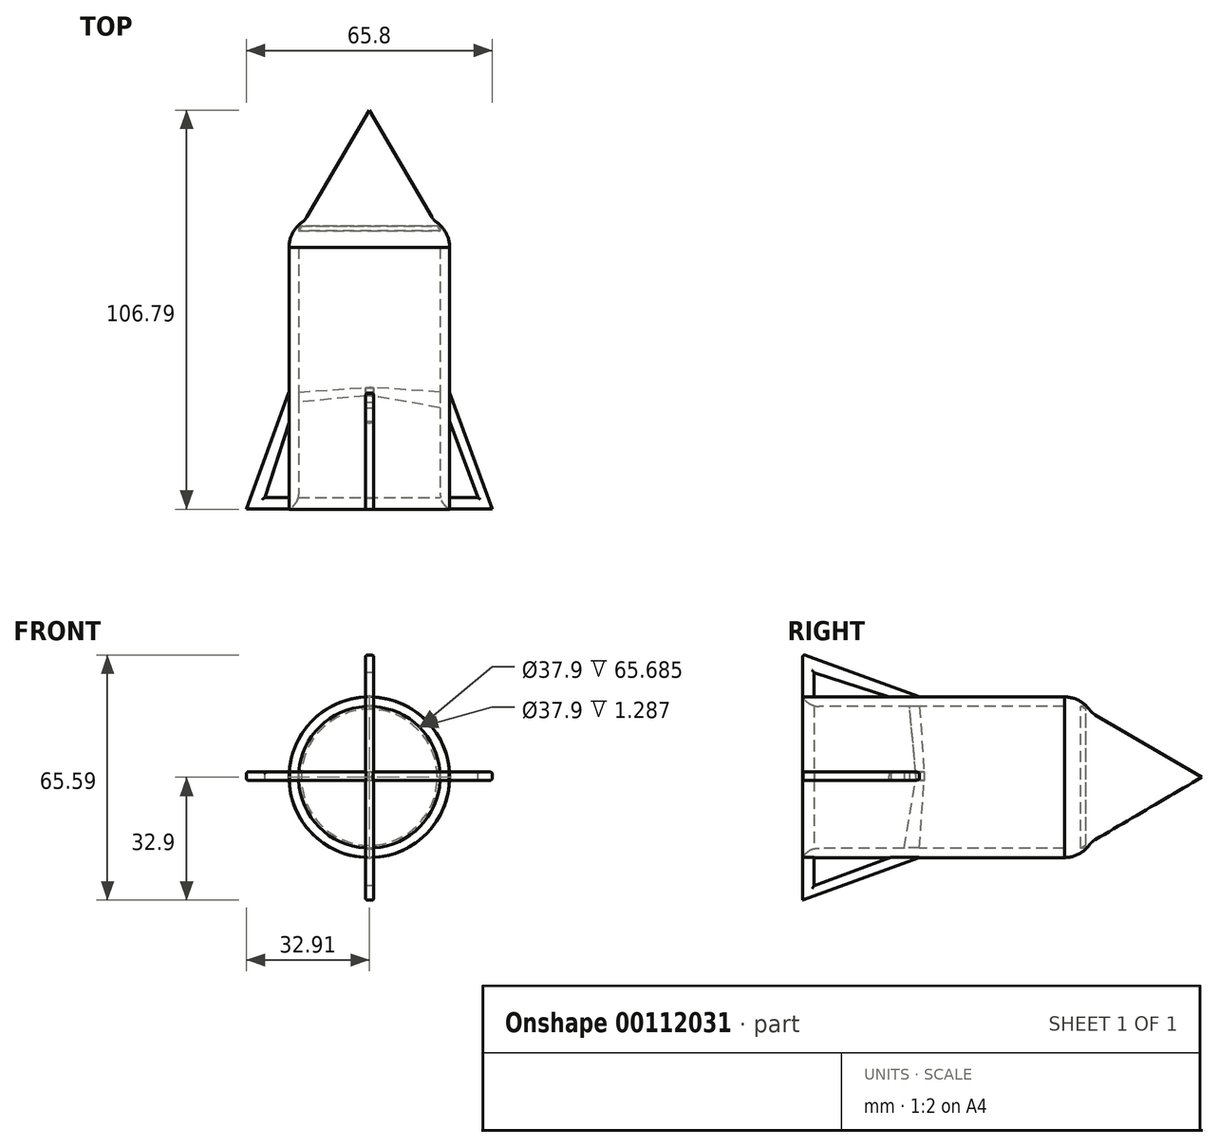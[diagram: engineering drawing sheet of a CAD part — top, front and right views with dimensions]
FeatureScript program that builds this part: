
annotation { "Feature Type Name" : "Feature", "Feature Type Description" : "" }
export const myFeature = defineFeature(function(context is Context, id is Id, definition is map)
    precondition{}
    {
        {
            var Q0;
            Q0=qCreatedBy(makeId("Front.planeOp"),FACE);
            var sketch = newSketch(context, id + "F0", { "sketchPlane" : qUnion([Q0])});
            skCircle(sketch, "E0", {"center": v(0, 0) * mm, "radius": 21.49 * mm});
            skSolve(sketch);
        }
        {
            var Q0;
            Q0 = qSketchRegion(id + "F0", true);
            extrude(context, id + "F1", {"entities" : qUnion([Q0]), "oppositeDirection" : true, "depth" : 78.3 * mm});
        }
        {
            var Q0;
            Q0=makeQuery(id+"F1.opExtrude","CAP_FACE",FACE,{"disambiguationData":[OSD([sQuery(id+"F0.wireOp",EDGE,"E0")])],"isStart":true});
            shell(context, id + "F2", {"entities" : qUnion([Q0]), "thickness" : 2.54 * mm});
        }
        {
            var Q0;
            {var subQ0=sQuery(id+"F0.wireOp",EDGE,"E0");Q0=makeQuery(id+"F2.opShell","OFFSET_EDGE",EDGE,{"disambiguationData":[OSD([subQ0]),TDD([makeQuery(id+"F1.opExtrude","CAP_EDGE",EDGE,{"disambiguationData":[OSD([subQ0])],"isStart":true})])]});}
            fillet(context, id + "F3", {"entities" : qUnion([Q0]), "radius" : 5.08 * mm, "tangentPropagation" : true, "allowEdgeOverflow" : false});
        }
        {
            var Q0;
            Q0=makeQuery(id+"F1.opExtrude","CAP_EDGE",EDGE,{"disambiguationData":[OSD([sQuery(id+"F0.wireOp",EDGE,"E0")])],"isStart":false});
            fillet(context, id + "F4", {"entities" : qUnion([Q0]), "radius" : 8.22 * mm, "tangentPropagation" : true, "allowEdgeOverflow" : false});
        }
        {
            var Q0;
            Q0=qCreatedBy(makeId("Right.planeOp"),FACE);
            var sketch = newSketch(context, id + "F5", { "sketchPlane" : qUnion([Q0])});
            skLineSegment(sketch, "E1", {"start": v(0, 0) * mm, "end": v(0, 32.9) * mm});
            skLineSegment(sketch, "E2", {"start": v(0, 32.9) * mm, "end": v(31.1, 21.54) * mm});
            skLineSegment(sketch, "E3", {"start": v(31.1, 21.54) * mm, "end": v(32.58, 0) * mm});
            skLineSegment(sketch, "E4", {"start": v(32.58, 0) * mm, "end": v(0, 0) * mm});
            skLineSegment(sketch, "E5.MirrorCS", {"start": v(0, -32.9) * mm, "end": v(31.1, -21.54) * mm});
            skLineSegment(sketch, "E6.MirrorCS", {"start": v(31.1, -21.54) * mm, "end": v(32.58, 0) * mm});
            skLineSegment(sketch, "E7.MirrorCS", {"start": v(0, 0) * mm, "end": v(0, -32.9) * mm});
            skLineSegment(sketch, "E8", {"start": v(28.54, 19.7) * mm, "end": v(3.06, 27.95) * mm});
            skLineSegment(sketch, "E9", {"start": v(3.06, 27.95) * mm, "end": v(3.06, -29.05) * mm});
            skLineSegment(sketch, "E10", {"start": v(3.06, -29.05) * mm, "end": v(26.9, -20.25) * mm});
            skLineSegment(sketch, "E11", {"start": v(26.9, -20.25) * mm, "end": v(30.38, 0) * mm});
            skLineSegment(sketch, "E12", {"start": v(30.38, 0) * mm, "end": v(28.54, 19.7) * mm});
            skSolve(sketch);
        }
        {
            var Q0;
            Q0 = qSketchRegion(id + "F5", true);
            var Q1;
            Q1=sQuery(id+"F5.wireOp",EDGE,"E1");
            var Q2;
            Q2=sQuery(id+"F5.wireOp",EDGE,"E2");
            var Q3;
            Q3=sQuery(id+"F5.wireOp",EDGE,"E6.MirrorCS");
            var Q4;
            Q4=sQuery(id+"F5.wireOp",EDGE,"E3");
            var Q5;
            Q5=sQuery(id+"F5.wireOp",EDGE,"E5.MirrorCS");
            var Q6;
            Q6=sQuery(id+"F5.wireOp",EDGE,"E7.MirrorCS");
            extrude(context, id + "F6", {"entities" : qUnion([Q0]), "operationType" : NewBodyOperationType.ADD, "surfaceEntities" : qUnion([Q1, Q2, Q3, Q4, Q5, Q6]), "depth" : 1.2 * mm, "hasSecondDirection" : true, "secondDirectionOppositeDirection" : true, "secondDirectionDepth" : 1.01 * mm});
        }
        {
            var Q0;
            Q0=qCreatedBy(makeId("Top.planeOp"),FACE);
            var sketch = newSketch(context, id + "F7", { "sketchPlane" : qUnion([Q0])});
            skLineSegment(sketch, "E13", {"start": v(-0.01, 0.1) * mm, "end": v(-32.91, 0.1) * mm});
            skLineSegment(sketch, "E14", {"start": v(-32.91, 0.1) * mm, "end": v(-21.55, 31.2) * mm});
            skLineSegment(sketch, "E15", {"start": v(-21.55, 31.2) * mm, "end": v(-0.01, 32.67) * mm});
            skLineSegment(sketch, "E16", {"start": v(-0.01, 32.67) * mm, "end": v(-0.01, 0.1) * mm});
            skLineSegment(sketch, "E17.MirrorCS", {"start": v(32.9, 0.1) * mm, "end": v(21.53, 31.2) * mm});
            skLineSegment(sketch, "E18.MirrorCS", {"start": v(21.53, 31.2) * mm, "end": v(-0.01, 32.67) * mm});
            skLineSegment(sketch, "E19.MirrorCS", {"start": v(-0.01, 0.1) * mm, "end": v(32.9, 0.1) * mm});
            skLineSegment(sketch, "E20", {"start": v(-19.72, 28.63) * mm, "end": v(-27.96, 3.16) * mm});
            skLineSegment(sketch, "E21", {"start": v(-27.96, 3.16) * mm, "end": v(29.04, 3.16) * mm});
            skLineSegment(sketch, "E22", {"start": v(29.04, 3.16) * mm, "end": v(20.24, 26.99) * mm});
            skLineSegment(sketch, "E23", {"start": v(20.24, 26.99) * mm, "end": v(-0.01, 30.47) * mm});
            skLineSegment(sketch, "E24", {"start": v(-0.01, 30.47) * mm, "end": v(-19.72, 28.63) * mm});
            skSolve(sketch);
        }
        {
            var Q0;
            Q0 = qSketchRegion(id + "F7", true);
            extrude(context, id + "F8", {"entities" : qUnion([Q0]), "operationType" : NewBodyOperationType.ADD, "oppositeDirection" : true, "depth" : 0.82 * mm, "hasSecondDirection" : true, "secondDirectionOppositeDirection" : false, "secondDirectionDepth" : 1.41 * mm});
        }
        {
            var Q0;
            Q0=qCreatedBy(makeId("Top.planeOp"),FACE);
            var sketch = newSketch(context, id + "F9", { "sketchPlane" : qUnion([Q0])});
            skLineSegment(sketch, "E25", {"start": v(-21.52, 70.08) * mm, "end": v(0, 70.08) * mm});
            skLineSegment(sketch, "E26", {"start": v(0, 70.08) * mm, "end": v(0, 106.8) * mm});
            skLineSegment(sketch, "E27", {"start": v(0, 106.8) * mm, "end": v(-21.52, 70.08) * mm});
            skSolve(sketch);
        }
        {
            var Q0;
            Q0 = qSketchRegion(id + "F9", true);
            var Q1;
            Q1=sQuery(id+"F9.wireOp",EDGE,"E26");
            revolve(context, id + "F10", {"operationType" : NewBodyOperationType.ADD, "entities" : qUnion([Q0]), "axis" : qUnion([Q1]), "revolveType" : RevolveType.FULL});
        }
        {
            var Q0;
            Q0=makeQuery(id+"F10.boolean.opBoolean","INTERSECT",EDGE,{"disambiguationData":[OD(0.0)],"derivedFrom":[makeQuery(id+"F4.opFillet","BLEND_FACE",FACE,{"disambiguationData":[OSD([sQuery(id+"F0.wireOp",EDGE,"E0")])]}),makeQuery(id+"F10.opRevolve","SWEPT_FACE",FACE,{"disambiguationData":[OSD([sQuery(id+"F9.wireOp",EDGE,"E27")])]})]});
            var Q1;
            Q1=makeQuery(id+"F10.boolean.opBoolean","INTERSECT",EDGE,{"disambiguationData":[OD(1.0)],"derivedFrom":[makeQuery(id+"F4.opFillet","BLEND_FACE",FACE,{"disambiguationData":[OSD([sQuery(id+"F0.wireOp",EDGE,"E0")])]}),makeQuery(id+"F10.opRevolve","SWEPT_FACE",FACE,{"disambiguationData":[OSD([sQuery(id+"F9.wireOp",EDGE,"E27")])]})]});
            fillet(context, id + "F11", {"entities" : qUnion([Q0, Q1]), "radius" : 5.08 * mm, "tangentPropagation" : true, "allowEdgeOverflow" : false});
        }
        {
            var Q0;
            {var subQ0=makeQuery(id+"F4.opFillet","BLEND_FACE",FACE,{"disambiguationData":[OSD([sQuery(id+"F0.wireOp",EDGE,"E0")])]});var subQ1=makeQuery(id+"F10.opRevolve","SWEPT_FACE",FACE,{"disambiguationData":[OSD([sQuery(id+"F9.wireOp",EDGE,"E27")])]});Q0=makeQuery(id+"F11.opFillet","BLEND_EDGE",EDGE,{"blendedFrom":[makeQuery(id+"F10.boolean.opBoolean","INTERSECT",EDGE,{"disambiguationData":[OD(1.0)],"derivedFrom":[subQ0,subQ1]}),makeQuery(id+"F10.boolean.opBoolean","SPLIT",FACE,{"disambiguationData":[TD([subQ0])],"derivedFrom":makeQuery(id+"F10.opRevolve","SWEPT_FACE",FACE,{"disambiguationData":[OSD([sQuery(id+"F9.wireOp",EDGE,"E25")])]})})],"blendedInto":[makeQuery(id+"F10.boolean.opBoolean","SPLIT",FACE,{"disambiguationData":[TD([subQ0])],"derivedFrom":makeQuery(id+"F10.opRevolve","SWEPT_FACE",FACE,{"disambiguationData":[OSD([sQuery(id+"F9.wireOp",EDGE,"E25")])]})})]});}
            fillet(context, id + "F12", {"entities" : qUnion([Q0]), "radius" : 5.08 * mm, "tangentPropagation" : true, "allowEdgeOverflow" : false});
        }
        {
            var Q0;
            Q0=makeQuery(id+"F6.opExtrude","CAP_EDGE",EDGE,{"disambiguationData":[OSD([sQuery(id+"F5.wireOp",EDGE,"E2")])],"isStart":false});
            var Q1;
            Q1=makeQuery(id+"F6.opExtrude","CAP_EDGE",EDGE,{"disambiguationData":[OSD([sQuery(id+"F5.wireOp",EDGE,"E2")])],"isStart":true});
            var Q2;
            Q2=makeQuery(id+"F6.opExtrude","SWEPT_FACE",FACE,{"disambiguationData":[OSD([sQuery(id+"F5.wireOp",EDGE,"E2")])]});
            var Q3;
            Q3=makeQuery(id+"F8.opExtrude","CAP_EDGE",EDGE,{"disambiguationData":[OSD([sQuery(id+"F7.wireOp",EDGE,"E17.MirrorCS")])],"isStart":true});
            var Q4;
            Q4=makeQuery(id+"F8.opExtrude","CAP_EDGE",EDGE,{"disambiguationData":[OSD([sQuery(id+"F7.wireOp",EDGE,"E17.MirrorCS")])],"isStart":false});
            var Q5;
            Q5=makeQuery(id+"F8.opExtrude","CAP_EDGE",EDGE,{"disambiguationData":[OSD([sQuery(id+"F7.wireOp",EDGE,"E14")])],"isStart":true});
            var Q6;
            Q6=makeQuery(id+"F8.opExtrude","CAP_EDGE",EDGE,{"disambiguationData":[OSD([sQuery(id+"F7.wireOp",EDGE,"E14")])],"isStart":false});
            var Q7;
            Q7=makeQuery(id+"F6.opExtrude","CAP_EDGE",EDGE,{"disambiguationData":[OSD([sQuery(id+"F5.wireOp",EDGE,"E5.MirrorCS")])],"isStart":false});
            var Q8;
            Q8=makeQuery(id+"F6.opExtrude","CAP_EDGE",EDGE,{"disambiguationData":[OSD([sQuery(id+"F5.wireOp",EDGE,"E5.MirrorCS")])],"isStart":true});
            var Q9;
            {var subQ0=sQuery(id+"F7.wireOp",EDGE,"E17.MirrorCS");var subQ1=sQuery(id+"F7.wireOp",EDGE,"E19.MirrorCS");var subQ2=sQuery(id+"F7.wireOp",EDGE,"E13");Q9=makeQuery(id+"F8.boolean.opBoolean","SPLIT",EDGE,{"disambiguationData":[TD([makeQuery(id+"F8.opExtrude","SWEPT_FACE",FACE,{"disambiguationData":[OSD([subQ0])]})])],"derivedFrom":makeQuery(id+"F8.opExtrude","CAP_EDGE",EDGE,{"disambiguationData":[OSD([subQ2,subQ1])],"isStart":true})});}
            var Q10;
            {var subQ0=sQuery(id+"F7.wireOp",EDGE,"E17.MirrorCS");var subQ1=sQuery(id+"F7.wireOp",EDGE,"E19.MirrorCS");var subQ2=sQuery(id+"F7.wireOp",EDGE,"E13");Q10=makeQuery(id+"F8.boolean.opBoolean","SPLIT",EDGE,{"disambiguationData":[TD([makeQuery(id+"F8.opExtrude","SWEPT_FACE",FACE,{"disambiguationData":[OSD([subQ0])]})])],"derivedFrom":makeQuery(id+"F8.opExtrude","CAP_EDGE",EDGE,{"disambiguationData":[OSD([subQ2,subQ1])],"isStart":false})});}
            var Q11;
            {var subQ0=sQuery(id+"F5.wireOp",EDGE,"E7.MirrorCS");var subQ1=sQuery(id+"F5.wireOp",EDGE,"E1");var subQ2=sQuery(id+"F5.wireOp",EDGE,"E2");var subQ3=sQuery(id+"F0.wireOp",EDGE,"E0");Q11=makeQuery(id+"F6.boolean.opBoolean","SPLIT",EDGE,{"disambiguationData":[TD([makeQuery(id+"F1.opExtrude","SWEPT_FACE",FACE,{"disambiguationData":[OSD([subQ3])]}),makeQuery(id+"F3.opFillet","BLEND_FACE",FACE,{"disambiguationData":[OSD([subQ3])]}),makeQuery(id+"F6.opExtrude","CAP_FACE",FACE,{"disambiguationData":[OSD([subQ1,subQ2,sQuery(id+"F5.wireOp",EDGE,"E3"),sQuery(id+"F5.wireOp",EDGE,"E6.MirrorCS"),subQ0,sQuery(id+"F5.wireOp",EDGE,"E5.MirrorCS"),sQuery(id+"F5.wireOp",EDGE,"E8"),sQuery(id+"F5.wireOp",EDGE,"E9"),sQuery(id+"F5.wireOp",EDGE,"E10"),sQuery(id+"F5.wireOp",EDGE,"E11"),sQuery(id+"F5.wireOp",EDGE,"E12")])],"isStart":false}),makeQuery(id+"F6.opExtrude","SWEPT_FACE",FACE,{"disambiguationData":[OSD([subQ1,subQ0])]}),makeQuery(id+"F6.opExtrude","SWEPT_FACE",FACE,{"disambiguationData":[OSD([subQ2])]})])],"derivedFrom":makeQuery(id+"F6.opExtrude","CAP_EDGE",EDGE,{"disambiguationData":[OSD([subQ1,subQ0])],"isStart":false})});}
            var Q12;
            {var subQ0=sQuery(id+"F5.wireOp",EDGE,"E7.MirrorCS");var subQ1=sQuery(id+"F5.wireOp",EDGE,"E1");var subQ2=sQuery(id+"F5.wireOp",EDGE,"E2");var subQ3=sQuery(id+"F0.wireOp",EDGE,"E0");Q12=makeQuery(id+"F6.boolean.opBoolean","SPLIT",EDGE,{"disambiguationData":[TD([makeQuery(id+"F1.opExtrude","SWEPT_FACE",FACE,{"disambiguationData":[OSD([subQ3])]}),makeQuery(id+"F3.opFillet","BLEND_FACE",FACE,{"disambiguationData":[OSD([subQ3])]}),makeQuery(id+"F6.opExtrude","CAP_FACE",FACE,{"disambiguationData":[OSD([subQ1,subQ2,sQuery(id+"F5.wireOp",EDGE,"E3"),sQuery(id+"F5.wireOp",EDGE,"E6.MirrorCS"),subQ0,sQuery(id+"F5.wireOp",EDGE,"E5.MirrorCS"),sQuery(id+"F5.wireOp",EDGE,"E8"),sQuery(id+"F5.wireOp",EDGE,"E9"),sQuery(id+"F5.wireOp",EDGE,"E10"),sQuery(id+"F5.wireOp",EDGE,"E11"),sQuery(id+"F5.wireOp",EDGE,"E12")])],"isStart":true}),makeQuery(id+"F6.opExtrude","SWEPT_FACE",FACE,{"disambiguationData":[OSD([subQ1,subQ0])]}),makeQuery(id+"F6.opExtrude","SWEPT_FACE",FACE,{"disambiguationData":[OSD([subQ2])]})])],"derivedFrom":makeQuery(id+"F6.opExtrude","CAP_EDGE",EDGE,{"disambiguationData":[OSD([subQ1,subQ0])],"isStart":true})});}
            var Q13;
            {var subQ0=sQuery(id+"F5.wireOp",EDGE,"E7.MirrorCS");var subQ1=sQuery(id+"F5.wireOp",EDGE,"E1");var subQ2=sQuery(id+"F5.wireOp",EDGE,"E5.MirrorCS");var subQ3=sQuery(id+"F0.wireOp",EDGE,"E0");Q13=makeQuery(id+"F6.boolean.opBoolean","SPLIT",EDGE,{"disambiguationData":[TD([makeQuery(id+"F1.opExtrude","SWEPT_FACE",FACE,{"disambiguationData":[OSD([subQ3])]}),makeQuery(id+"F3.opFillet","BLEND_FACE",FACE,{"disambiguationData":[OSD([subQ3])]}),makeQuery(id+"F6.opExtrude","CAP_FACE",FACE,{"disambiguationData":[OSD([subQ1,sQuery(id+"F5.wireOp",EDGE,"E2"),sQuery(id+"F5.wireOp",EDGE,"E3"),sQuery(id+"F5.wireOp",EDGE,"E6.MirrorCS"),subQ0,subQ2,sQuery(id+"F5.wireOp",EDGE,"E8"),sQuery(id+"F5.wireOp",EDGE,"E9"),sQuery(id+"F5.wireOp",EDGE,"E10"),sQuery(id+"F5.wireOp",EDGE,"E11"),sQuery(id+"F5.wireOp",EDGE,"E12")])],"isStart":true}),makeQuery(id+"F6.opExtrude","SWEPT_FACE",FACE,{"disambiguationData":[OSD([subQ1,subQ0])]}),makeQuery(id+"F6.opExtrude","SWEPT_FACE",FACE,{"disambiguationData":[OSD([subQ2])]})])],"derivedFrom":makeQuery(id+"F6.opExtrude","CAP_EDGE",EDGE,{"disambiguationData":[OSD([subQ1,subQ0])],"isStart":true})});}
            var Q14;
            {var subQ0=sQuery(id+"F7.wireOp",EDGE,"E19.MirrorCS");var subQ1=sQuery(id+"F7.wireOp",EDGE,"E14");var subQ2=sQuery(id+"F7.wireOp",EDGE,"E13");Q14=makeQuery(id+"F8.boolean.opBoolean","SPLIT",EDGE,{"disambiguationData":[TD([makeQuery(id+"F8.opExtrude","SWEPT_FACE",FACE,{"disambiguationData":[OSD([subQ1])]})])],"derivedFrom":makeQuery(id+"F8.opExtrude","CAP_EDGE",EDGE,{"disambiguationData":[OSD([subQ2,subQ0])],"isStart":false})});}
            var Q15;
            Q15=makeQuery(id+"F6.opExtrude","CAP_EDGE",EDGE,{"disambiguationData":[OSD([sQuery(id+"F5.wireOp",EDGE,"E8")])],"isStart":false});
            var Q16;
            Q16=makeQuery(id+"F8.opExtrude","CAP_EDGE",EDGE,{"disambiguationData":[OSD([sQuery(id+"F7.wireOp",EDGE,"E22")])],"isStart":true});
            var Q17;
            Q17=makeQuery(id+"F8.opExtrude","CAP_EDGE",EDGE,{"disambiguationData":[OSD([sQuery(id+"F7.wireOp",EDGE,"E22")])],"isStart":false});
            var Q18;
            {var subQ0=sQuery(id+"F7.wireOp",EDGE,"E21");var subQ1=sQuery(id+"F7.wireOp",EDGE,"E22");Q18=makeQuery(id+"F8.boolean.opBoolean","SPLIT",EDGE,{"disambiguationData":[TD([makeQuery(id+"F8.opExtrude","SWEPT_FACE",FACE,{"disambiguationData":[OSD([subQ1])]})])],"derivedFrom":makeQuery(id+"F8.opExtrude","CAP_EDGE",EDGE,{"disambiguationData":[OSD([subQ0])],"isStart":false})});}
            var Q19;
            {var subQ0=sQuery(id+"F5.wireOp",EDGE,"E9");var subQ1=sQuery(id+"F5.wireOp",EDGE,"E8");Q19=makeQuery(id+"F6.boolean.opBoolean","SPLIT",EDGE,{"disambiguationData":[TD([makeQuery(id+"F6.opExtrude","SWEPT_FACE",FACE,{"disambiguationData":[OSD([subQ1])]})])],"derivedFrom":makeQuery(id+"F6.opExtrude","CAP_EDGE",EDGE,{"disambiguationData":[OSD([subQ0])],"isStart":true})});}
            var Q20;
            {var subQ0=sQuery(id+"F5.wireOp",EDGE,"E9");var subQ1=sQuery(id+"F5.wireOp",EDGE,"E8");Q20=makeQuery(id+"F6.boolean.opBoolean","SPLIT",EDGE,{"disambiguationData":[TD([makeQuery(id+"F6.opExtrude","SWEPT_FACE",FACE,{"disambiguationData":[OSD([subQ1])]})])],"derivedFrom":makeQuery(id+"F6.opExtrude","CAP_EDGE",EDGE,{"disambiguationData":[OSD([subQ0])],"isStart":false})});}
            var Q21;
            {var subQ0=sQuery(id+"F7.wireOp",EDGE,"E21");var subQ1=sQuery(id+"F7.wireOp",EDGE,"E22");Q21=makeQuery(id+"F8.boolean.opBoolean","SPLIT",EDGE,{"disambiguationData":[TD([makeQuery(id+"F8.opExtrude","SWEPT_FACE",FACE,{"disambiguationData":[OSD([subQ1])]})])],"derivedFrom":makeQuery(id+"F8.opExtrude","CAP_EDGE",EDGE,{"disambiguationData":[OSD([subQ0])],"isStart":true})});}
            var Q22;
            {var subQ0=sQuery(id+"F7.wireOp",EDGE,"E21");var subQ1=sQuery(id+"F7.wireOp",EDGE,"E20");Q22=makeQuery(id+"F8.boolean.opBoolean","SPLIT",EDGE,{"disambiguationData":[TD([makeQuery(id+"F8.opExtrude","SWEPT_FACE",FACE,{"disambiguationData":[OSD([subQ1])]})])],"derivedFrom":makeQuery(id+"F8.opExtrude","CAP_EDGE",EDGE,{"disambiguationData":[OSD([subQ0])],"isStart":true})});}
            var Q23;
            Q23=makeQuery(id+"F8.opExtrude","CAP_EDGE",EDGE,{"disambiguationData":[OSD([sQuery(id+"F7.wireOp",EDGE,"E20")])],"isStart":true});
            var Q24;
            {var subQ0=sQuery(id+"F5.wireOp",EDGE,"E9");var subQ1=sQuery(id+"F5.wireOp",EDGE,"E10");Q24=makeQuery(id+"F6.boolean.opBoolean","SPLIT",EDGE,{"disambiguationData":[TD([makeQuery(id+"F6.opExtrude","SWEPT_FACE",FACE,{"disambiguationData":[OSD([subQ1])]})])],"derivedFrom":makeQuery(id+"F6.opExtrude","CAP_EDGE",EDGE,{"disambiguationData":[OSD([subQ0])],"isStart":false})});}
            var Q25;
            {var subQ0=sQuery(id+"F5.wireOp",EDGE,"E9");var subQ1=sQuery(id+"F5.wireOp",EDGE,"E10");Q25=makeQuery(id+"F6.boolean.opBoolean","SPLIT",EDGE,{"disambiguationData":[TD([makeQuery(id+"F6.opExtrude","SWEPT_FACE",FACE,{"disambiguationData":[OSD([subQ1])]})])],"derivedFrom":makeQuery(id+"F6.opExtrude","CAP_EDGE",EDGE,{"disambiguationData":[OSD([subQ0])],"isStart":true})});}
            var Q26;
            Q26=makeQuery(id+"F6.opExtrude","CAP_EDGE",EDGE,{"disambiguationData":[OSD([sQuery(id+"F5.wireOp",EDGE,"E10")])],"isStart":false});
            var Q27;
            {var subQ0=sQuery(id+"F5.wireOp",EDGE,"E7.MirrorCS");var subQ1=sQuery(id+"F5.wireOp",EDGE,"E1");var subQ2=sQuery(id+"F5.wireOp",EDGE,"E5.MirrorCS");var subQ3=sQuery(id+"F0.wireOp",EDGE,"E0");Q27=makeQuery(id+"F6.boolean.opBoolean","SPLIT",EDGE,{"disambiguationData":[TD([makeQuery(id+"F1.opExtrude","SWEPT_FACE",FACE,{"disambiguationData":[OSD([subQ3])]}),makeQuery(id+"F3.opFillet","BLEND_FACE",FACE,{"disambiguationData":[OSD([subQ3])]}),makeQuery(id+"F6.opExtrude","CAP_FACE",FACE,{"disambiguationData":[OSD([subQ1,sQuery(id+"F5.wireOp",EDGE,"E2"),sQuery(id+"F5.wireOp",EDGE,"E3"),sQuery(id+"F5.wireOp",EDGE,"E6.MirrorCS"),subQ0,subQ2,sQuery(id+"F5.wireOp",EDGE,"E8"),sQuery(id+"F5.wireOp",EDGE,"E9"),sQuery(id+"F5.wireOp",EDGE,"E10"),sQuery(id+"F5.wireOp",EDGE,"E11"),sQuery(id+"F5.wireOp",EDGE,"E12")])],"isStart":false}),makeQuery(id+"F6.opExtrude","SWEPT_FACE",FACE,{"disambiguationData":[OSD([subQ1,subQ0])]}),makeQuery(id+"F6.opExtrude","SWEPT_FACE",FACE,{"disambiguationData":[OSD([subQ2])]})])],"derivedFrom":makeQuery(id+"F6.opExtrude","CAP_EDGE",EDGE,{"disambiguationData":[OSD([subQ1,subQ0])],"isStart":false})});}
            var Q28;
            Q28=makeQuery(id+"F6.opExtrude","CAP_EDGE",EDGE,{"disambiguationData":[OSD([sQuery(id+"F5.wireOp",EDGE,"E10")])],"isStart":true});
            var Q29;
            {var subQ0=sQuery(id+"F7.wireOp",EDGE,"E21");var subQ1=sQuery(id+"F7.wireOp",EDGE,"E20");Q29=makeQuery(id+"F8.boolean.opBoolean","SPLIT",EDGE,{"disambiguationData":[TD([makeQuery(id+"F8.opExtrude","SWEPT_FACE",FACE,{"disambiguationData":[OSD([subQ1])]})])],"derivedFrom":makeQuery(id+"F8.opExtrude","CAP_EDGE",EDGE,{"disambiguationData":[OSD([subQ0])],"isStart":false})});}
            var Q30;
            Q30=makeQuery(id+"F8.opExtrude","CAP_EDGE",EDGE,{"disambiguationData":[OSD([sQuery(id+"F7.wireOp",EDGE,"E20")])],"isStart":false});
            var Q31;
            Q31=makeQuery(id+"F6.opExtrude","CAP_EDGE",EDGE,{"disambiguationData":[OSD([sQuery(id+"F5.wireOp",EDGE,"E8")])],"isStart":true});
            fillet(context, id + "F13", {"entities" : qUnion([Q0, Q1, Q2, Q3, Q4, Q5, Q6, Q7, Q8, Q9, Q10, Q11, Q12, Q13, Q14, Q15, Q16, Q17, Q18, Q19, Q20, Q21, Q22, Q23, Q24, Q25, Q26, Q27, Q28, Q29, Q30, Q31]), "radius" : 0.48 * mm, "tangentPropagation" : true, "allowEdgeOverflow" : false});
        }
    });
